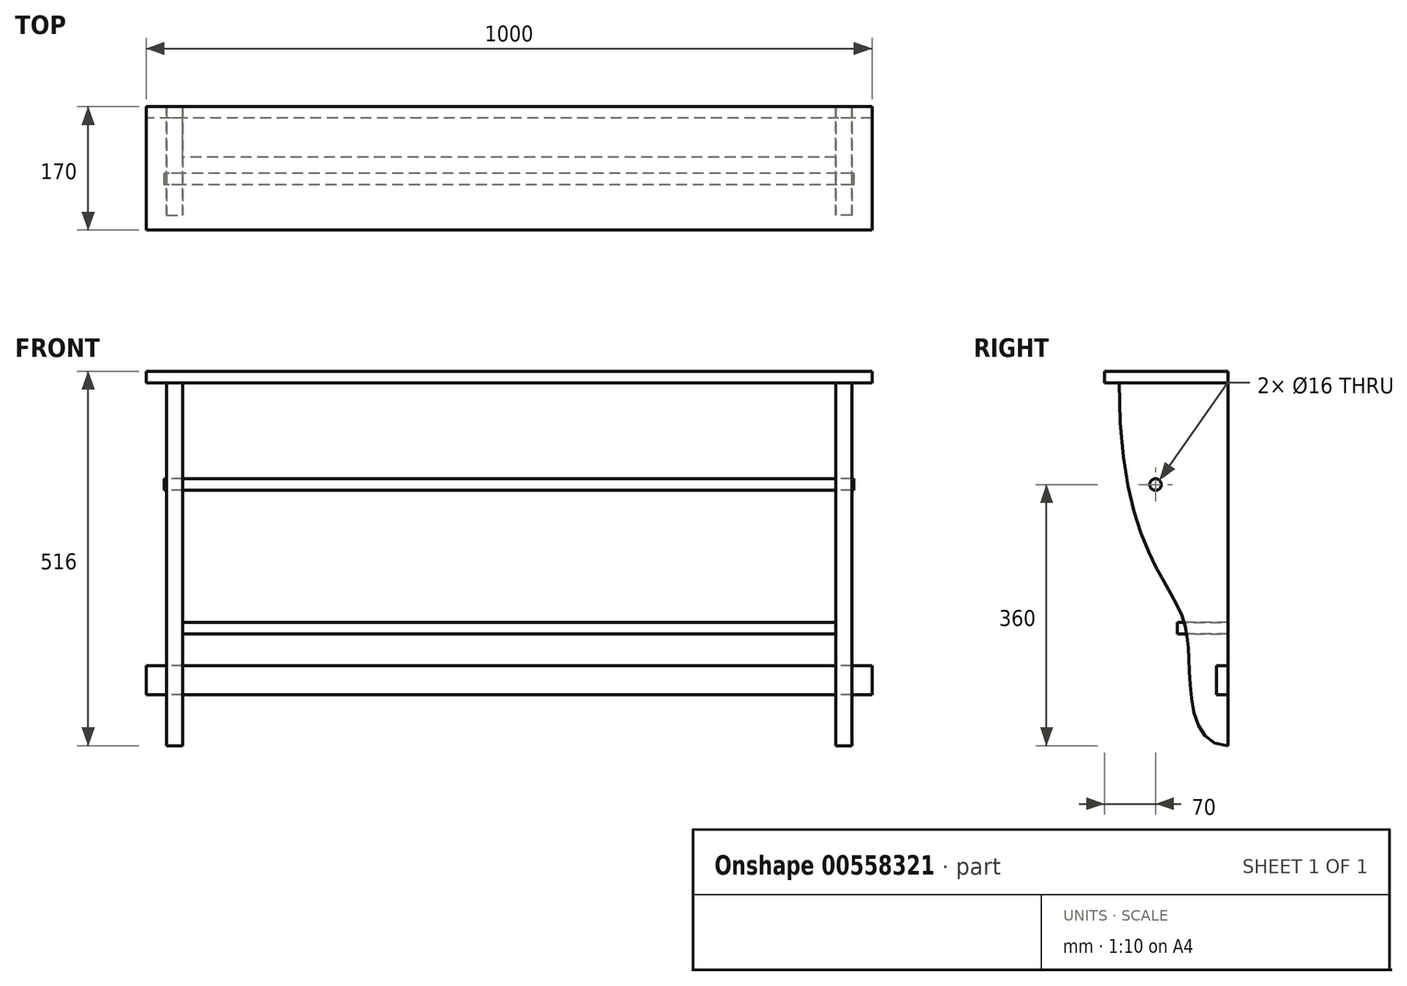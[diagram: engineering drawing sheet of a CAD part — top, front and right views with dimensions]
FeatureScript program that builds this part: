
annotation { "Feature Type Name" : "Feature", "Feature Type Description" : "" }
export const myFeature = defineFeature(function(context is Context, id is Id, definition is map)
    precondition{}
    {
        {
            var Q0;
            Q0=qCreatedBy(makeId("Right.planeOp"),FACE);
            cPlane(context, id + "F0", {"entities" : qUnion([Q0]), "cplaneType" : CPlaneType.OFFSET, "offset" : 450 * mm, "width" : 150 * mm, "height" : 150 * mm});
        }
        {
            var Q0;
            Q0=qCreatedBy(id+"F0.planeOp",FACE);
            var sketch = newSketch(context, id + "F1", { "sketchPlane" : qUnion([Q0])});
            skLineSegment(sketch, "E0", {"start": v(-150, 250) * mm, "end": v(0, 250) * mm});
            skLineSegment(sketch, "E1", {"start": v(0, 250) * mm, "end": v(0, -250) * mm});
            skFitSpline(sketch, "E2", {"points": [v(0, -250) * mm, v(-52.36, -164.2) * mm, v(-63.4, -71.82) * mm, v(-150, 250) * mm], "startDerivative": vector(-484.2, 0) * mm, "endDerivative": vector(0, 1332.97) * mm});
            skSolve(sketch);
        }
        {
            var Q0;
            Q0 = qSketchRegion(id + "F1", true);
            extrude(context, id + "F2", {"entities" : qUnion([Q0]), "depth" : 22 * mm, "offsetDistance" : 25 * mm});
        }
        {
            var Q0;
            Q0=makeQuery(id+"F2.opExtrude","SWEPT_BODY",BODY,{"disambiguationData":[OSD([sQuery(id+"F1.wireOp",EDGE,"E0"),sQuery(id+"F1.wireOp",EDGE,"E1"),sQuery(id+"F1.wireOp",EDGE,"E2")])]});
            var Q1;
            Q1=qCreatedBy(makeId("Right.planeOp"),FACE);
            mirror(context, id + "F3", {"entities" : qUnion([Q0]), "mirrorPlane" : qUnion([Q1])});
        }
        {
            var Q0;
            Q0=makeQuery(id+"F2.opExtrude","SWEPT_FACE",FACE,{"disambiguationData":[OSD([sQuery(id+"F1.wireOp",EDGE,"E0")])]});
            var sketch = newSketch(context, id + "F4", { "sketchPlane" : qUnion([Q0])});
            skLineSegment(sketch, "E3.bottom", {"start": v(-500, 0) * mm, "end": v(500, 0) * mm});
            skLineSegment(sketch, "E3.top", {"start": v(-500, -170) * mm, "end": v(500, -170) * mm});
            skLineSegment(sketch, "E3.left", {"start": v(-500, 0) * mm, "end": v(-500, -170) * mm});
            skLineSegment(sketch, "E3.right", {"start": v(500, 0) * mm, "end": v(500, -170) * mm});
            skSolve(sketch);
        }
        {
            var Q0;
            Q0 = qSketchRegion(id + "F4", true);
            extrude(context, id + "F5", {"entities" : qUnion([Q0]), "depth" : 16 * mm, "offsetDistance" : 25 * mm});
        }
        {
            var Q0;
            Q0=qCreatedBy(makeId("Right.planeOp"),FACE);
            var sketch = newSketch(context, id + "F6", { "sketchPlane" : qUnion([Q0])});
            skLineSegment(sketch, "E4.bottom", {"start": v(0, -140) * mm, "end": v(-16, -140) * mm});
            skLineSegment(sketch, "E4.top", {"start": v(0, -180) * mm, "end": v(-16, -180) * mm});
            skLineSegment(sketch, "E4.left", {"start": v(0, -140) * mm, "end": v(0, -180) * mm});
            skLineSegment(sketch, "E4.right", {"start": v(-16, -140) * mm, "end": v(-16, -180) * mm});
            skSolve(sketch);
        }
        {
            var Q0;
            Q0 = qSketchRegion(id + "F6", true);
            extrude(context, id + "F7", {"entities" : qUnion([Q0]), "endBound" : BoundingType.SYMMETRIC, "depth" : 1000 * mm, "offsetDistance" : 25 * mm});
        }
        {
            var Q0;
            Q0=qCreatedBy(makeId("Right.planeOp"),FACE);
            var sketch = newSketch(context, id + "F8", { "sketchPlane" : qUnion([Q0])});
            skLineSegment(sketch, "E5.bottom", {"start": v(0, -80) * mm, "end": v(-70, -80) * mm});
            skLineSegment(sketch, "E5.top", {"start": v(0, -96) * mm, "end": v(-70, -96) * mm});
            skLineSegment(sketch, "E5.left", {"start": v(0, -80) * mm, "end": v(0, -96) * mm});
            skLineSegment(sketch, "E5.right", {"start": v(-70, -80) * mm, "end": v(-70, -96) * mm});
            skSolve(sketch);
        }
        {
            var Q0;
            Q0 = qSketchRegion(id + "F8", true);
            var Q1;
            Q1=makeQuery(id+"F2.opExtrude","CAP_FACE",FACE,{"disambiguationData":[OSD([sQuery(id+"F1.wireOp",EDGE,"E0"),sQuery(id+"F1.wireOp",EDGE,"E1"),sQuery(id+"F1.wireOp",EDGE,"E2")])],"isStart":true});
            var Q2;
            Q2=makeQuery(id+"F2.opExtrude","SWEPT_BODY",BODY,{"disambiguationData":[OSD([sQuery(id+"F1.wireOp",EDGE,"E0"),sQuery(id+"F1.wireOp",EDGE,"E1"),sQuery(id+"F1.wireOp",EDGE,"E2")])]});
            var Q3;
            Q3=makeQuery(id+"F3.opPattern","COPY",FACE,{"derivedFrom":makeQuery(id+"F2.opExtrude","CAP_FACE",FACE,{"disambiguationData":[OSD([sQuery(id+"F1.wireOp",EDGE,"E0"),sQuery(id+"F1.wireOp",EDGE,"E1"),sQuery(id+"F1.wireOp",EDGE,"E2")])],"isStart":true}),"instanceName":"1"});
            extrude(context, id + "F9", {"entities" : qUnion([Q0]), "endBound" : BoundingType.UP_TO_SURFACE, "depth" : 25 * mm, "endBoundEntityFace" : qUnion([Q1]), "endBoundEntityBody" : qUnion([Q2]), "offsetDistance" : 25 * mm, "hasSecondDirection" : true, "secondDirectionBound" : SecondDirectionBoundingType.UP_TO_SURFACE, "secondDirectionOppositeDirection" : true, "secondDirectionDepth" : 25 * mm, "secondDirectionBoundEntityFace" : qUnion([Q3])});
        }
        {
            var Q0;
            Q0=qCreatedBy(makeId("Right.planeOp"),FACE);
            var sketch = newSketch(context, id + "F10", { "sketchPlane" : qUnion([Q0])});
            skCircle(sketch, "E6", {"center": v(-100, 110) * mm, "radius": 8 * mm});
            skSolve(sketch);
        }
        {
            var Q0;
            Q0 = qSketchRegion(id + "F10", true);
            var Q1;
            Q1=makeQuery(id+"F2.opExtrude","CAP_FACE",FACE,{"disambiguationData":[OSD([sQuery(id+"F1.wireOp",EDGE,"E0"),sQuery(id+"F1.wireOp",EDGE,"E1"),sQuery(id+"F1.wireOp",EDGE,"E2")])],"isStart":true});
            var Q2;
            Q2=makeQuery(id+"F3.opPattern","COPY",FACE,{"derivedFrom":makeQuery(id+"F2.opExtrude","CAP_FACE",FACE,{"disambiguationData":[OSD([sQuery(id+"F1.wireOp",EDGE,"E0"),sQuery(id+"F1.wireOp",EDGE,"E1"),sQuery(id+"F1.wireOp",EDGE,"E2")])],"isStart":true}),"instanceName":"1"});
            extrude(context, id + "F11", {"entities" : qUnion([Q0]), "endBound" : BoundingType.SYMMETRIC, "depth" : 950 * mm, "endBoundEntityFace" : qUnion([Q1]), "offsetDistance" : 25 * mm, "hasSecondDirection" : true, "secondDirectionBound" : SecondDirectionBoundingType.UP_TO_SURFACE, "secondDirectionOppositeDirection" : true, "secondDirectionDepth" : 25 * mm, "secondDirectionBoundEntityFace" : qUnion([Q2])});
        }
        {
            var Q0;
            Q0=makeQuery(id+"F7.opExtrude","SWEPT_BODY",BODY,{"disambiguationData":[OSD([sQuery(id+"F6.wireOp",EDGE,"E4.bottom"),sQuery(id+"F6.wireOp",EDGE,"E4.top"),sQuery(id+"F6.wireOp",EDGE,"E4.left"),sQuery(id+"F6.wireOp",EDGE,"E4.right")])]});
            var Q1;
            Q1=makeQuery(id+"F3.opPattern","COPY",BODY,{"derivedFrom":makeQuery(id+"F2.opExtrude","SWEPT_BODY",BODY,{"disambiguationData":[OSD([sQuery(id+"F1.wireOp",EDGE,"E0"),sQuery(id+"F1.wireOp",EDGE,"E1"),sQuery(id+"F1.wireOp",EDGE,"E2")])]}),"instanceName":"1"});
            var Q2;
            Q2=makeQuery(id+"F2.opExtrude","SWEPT_BODY",BODY,{"disambiguationData":[OSD([sQuery(id+"F1.wireOp",EDGE,"E0"),sQuery(id+"F1.wireOp",EDGE,"E1"),sQuery(id+"F1.wireOp",EDGE,"E2")])]});
            booleanBodies(context, id + "F12", {"operationType" : BooleanOperationType.SUBTRACTION, "tools" : qUnion([Q0]), "targets" : qUnion([Q1, Q2]), "keepTools" : true});
        }
        {
            var Q0;
            Q0=makeQuery(id+"F11.opExtrude","SWEPT_BODY",BODY,{"disambiguationData":[OSD([sQuery(id+"F10.wireOp",EDGE,"E6")])]});
            var Q1;
            Q1=makeQuery(id+"F3.opPattern","COPY",BODY,{"derivedFrom":makeQuery(id+"F2.opExtrude","SWEPT_BODY",BODY,{"disambiguationData":[OSD([sQuery(id+"F1.wireOp",EDGE,"E0"),sQuery(id+"F1.wireOp",EDGE,"E1"),sQuery(id+"F1.wireOp",EDGE,"E2")])]}),"instanceName":"1"});
            var Q2;
            Q2=makeQuery(id+"F2.opExtrude","SWEPT_BODY",BODY,{"disambiguationData":[OSD([sQuery(id+"F1.wireOp",EDGE,"E0"),sQuery(id+"F1.wireOp",EDGE,"E1"),sQuery(id+"F1.wireOp",EDGE,"E2")])]});
            booleanBodies(context, id + "F13", {"operationType" : BooleanOperationType.SUBTRACTION, "tools" : qUnion([Q0]), "targets" : qUnion([Q1, Q2]), "keepTools" : true});
        }
    });
